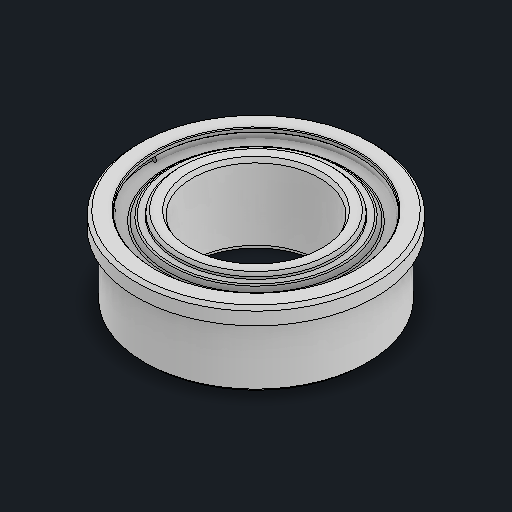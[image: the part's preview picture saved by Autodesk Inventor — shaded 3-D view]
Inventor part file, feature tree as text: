
AUTODESK INVENTOR PART (.ipt)
format: ipt  version: 2024 (Build 280153000, 153)  size: 258,048 bytes
history: native  units: in
note: dims shown in document units (in); Inventor stores cm internally (conversion verified against a paired STEP export)
features: chamfer x1, revolve x1, mirror x1
ambient origin geometry x8: Origin, YZ Plane, XZ Plane, XY Plane, X Axis, Y Axis, Z Axis, Center Point
bodies: Solid1 (feature_tree), Solid2 (feature_tree), Solid3 (feature_tree)
feature tree (3):
  chamfer  "Chamfer7"  [1 undecoded]
  revolve  "Revolve1"  [1 undecoded]
  mirror  "Mirror3"
note: 2 required parameter values undecoded (feature->parameter linkage not recoverable at this tier; creation-order binding heuristic only, values carry confidence <= 0.55)
